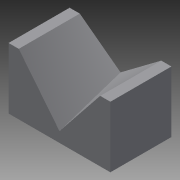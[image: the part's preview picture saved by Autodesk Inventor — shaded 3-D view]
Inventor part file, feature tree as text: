
AUTODESK INVENTOR PART (.ipt)
format: ipt  version: 2015 (Build 190159000, 159)  size: 101,888 bytes
history: native  units: in
note: dims shown in document units (in); Inventor stores cm internally (conversion verified against a paired STEP export)
features: sketch x3, extrude x1, loft x1
ambient origin geometry x8: Origin, YZ Plane, XZ Plane, XY Plane, X Axis, Y Axis, Z Axis, Center Point
bodies: Solid1 (feature_tree)
feature tree (5):
  extrude  "Extrusion1"  Depth=2.5in
  loft  "Loft1"
  sketch  "Sketch1"  dims[d0=1.5in d1=2.5in]
  sketch  "Sketch2"  dims[d2=1.5in d3=0.0in d4=0.25in]
  sketch  "Sketch3"  dims[d5=0.25in d8=0.25in d9=0.25in d10=0.75in d11=1.25in d12=0.0in d13=90.0deg d14=0.0in d15=90.0deg]
